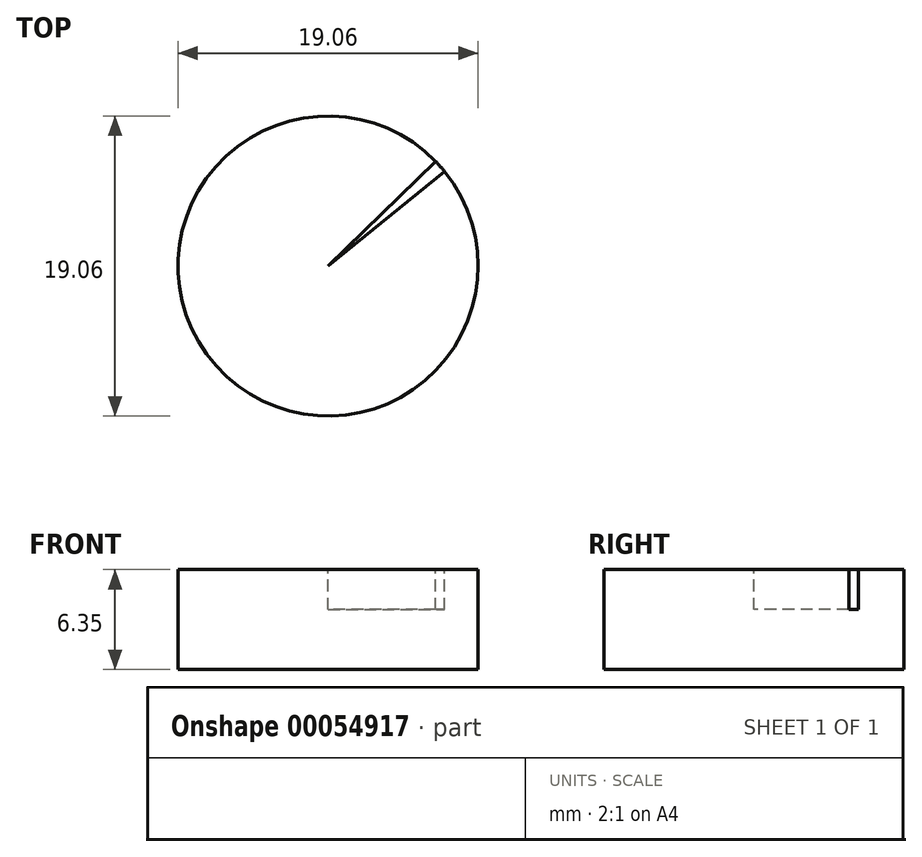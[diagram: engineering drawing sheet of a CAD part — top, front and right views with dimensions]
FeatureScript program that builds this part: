
annotation { "Feature Type Name" : "Feature", "Feature Type Description" : "" }
export const myFeature = defineFeature(function(context is Context, id is Id, definition is map)
    precondition{}
    {
        {
            var Q0;
            Q0=qCreatedBy(makeId("Top.planeOp"),FACE);
            var sketch = newSketch(context, id + "F0", { "sketchPlane" : qUnion([Q0])});
            skCircle(sketch, "E0", {"center": v(0, 0) * mm, "radius": 9.53 * mm});
            skSolve(sketch);
        }
        {
            var Q0;
            Q0=makeQuery(id+"F0.imprint","IMPRINT",FACE,{"disambiguationData":[TD([[makeQuery(id+"F0.imprint","IMPRINT",EDGE,{"derivedFrom":sQuery(id+"F0.wireOp",EDGE,"E0")}),1.0]])]});
            extrude(context, id + "F1", {"entities" : qUnion([Q0]), "depth" : 6.35 * mm});
        }
        {
            var Q0;
            Q0=makeQuery(id+"F1.opExtrude","CAP_FACE",FACE,{"disambiguationData":[OSD([sQuery(id+"F0.wireOp",EDGE,"E0")])],"isStart":false});
            var sketch = newSketch(context, id + "F2", { "sketchPlane" : qUnion([Q0])});
            skLineSegment(sketch, "E1", {"start": v(6.84, 6.63) * mm, "end": v(0, 0) * mm});
            skLineSegment(sketch, "E2", {"start": v(0, 0) * mm, "end": v(7.4, 6) * mm});
            skSolve(sketch);
        }
        {
            var Q0;
            {var subQ0=sQuery(id+"F2.wireOp",EDGE,"E1");Q0=makeQuery(id+"F2.imprint","IMPRINT",FACE,{"disambiguationData":[TD([[makeQuery(id+"F2.imprint","IMPRINT",EDGE,{"derivedFrom":subQ0}),1.0]])]});}
            extrude(context, id + "F3", {"entities" : qUnion([Q0]), "operationType" : NewBodyOperationType.REMOVE, "oppositeDirection" : true, "depth" : 2.54 * mm});
        }
    });
